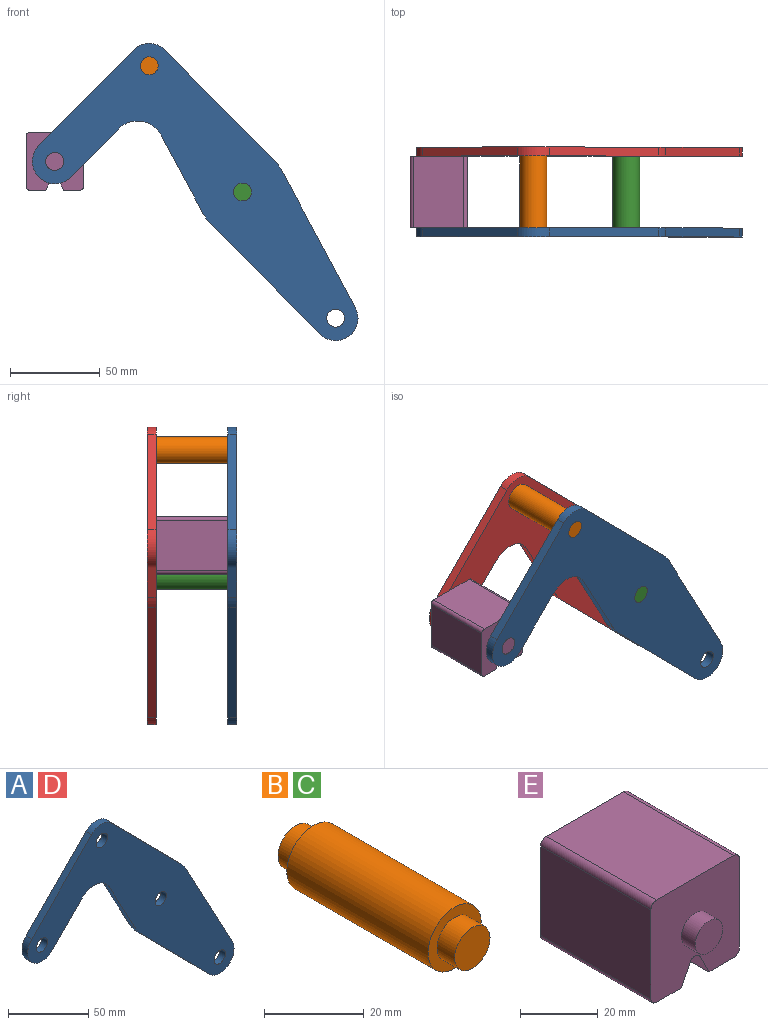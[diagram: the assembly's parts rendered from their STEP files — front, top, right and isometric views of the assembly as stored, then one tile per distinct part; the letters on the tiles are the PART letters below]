
ASSEMBLY  parts=5 mates=3
PART A: 18 faces, bbox 181.7x5x165.8 mm
  f0: plane 43.49x23.35mm, normal (-0.88,0,-0.47), area 246.8mm2, adj f1,f14,f16,f17
  f1: cylinder r=25mm len=5.75mm, axis (0,1,0), area 35.8mm2, adj f0,f2,f16,f17
  f2: plane 61.6x60.87mm, normal (-0.71,0,-0.7), area 433mm2, adj f1,f3,f16,f17
  f3: cylinder r=12.5mm len=21.39mm, axis (0,1,0), area 178.4mm2, adj f2,f4,f16,f17
  f4: plane 76.3x40.96mm, normal (0.88,0,0.47), area 433mm2, adj f3,f5,f16,f17
  f5: cylinder r=25mm len=5.75mm, axis (0,1,0), area 35.8mm2, adj f4,f6,f16,f17
  f6: plane 61.6x60.87mm, normal (0.71,0,0.7), area 433mm2, adj f5,f7,f16,f17
  f7: cylinder r=12.5mm len=17.78mm, axis (0,1,0), area 98.9mm2, adj f6,f8,f16,f17
  f8: plane 53.35x52.71mm, normal (-0.71,0,0.7), area 375mm2, adj f7,f9,f16,f17
  f9: cylinder r=12.5mm len=21.39mm, axis (0,1,0), area 196.3mm2, adj f8,f10,f16,f17
  f10: plane 26.86x26.54mm, normal (0.71,0,-0.7), area 188.8mm2, adj f9,f14,f16,f17
  f11: cylinder r=5mm len=10mm, axis (0,1,0), area 157.1mm2, adj f16,f17
  f12: cylinder r=5mm len=10mm, axis (0,1,0), area 157.1mm2, adj f16,f17
  f13: cylinder r=5mm len=10mm, axis (0,1,0), area 157.1mm2, adj f16,f17
  f14: cylinder r=15mm len=23.89mm, axis (0,1,0), area 140.2mm2, adj f0,f10,f16,f17
  f15: cylinder r=5mm len=10mm, axis (0,1,0), area 157.1mm2, adj f16,f17
  f16: plane 181.66x165.78mm, normal (0,-1,0), area 8710.1mm2, adj f0,f1,f2,f3,f4,f5,f6,f7
  f17: plane 181.66x165.78mm, normal (0,1,0), area 8710.1mm2, adj f0,f1,f2,f3,f4,f5,f6,f7
PART B: 7 faces, bbox 15x50x15 mm
  f0: cylinder r=7.5mm len=40mm, axis (0,-1,0), area 1885mm2, adj f2,f5
  f1: cylinder r=5mm len=10mm, axis (0,1,0), area 157.1mm2, adj f2,f3
  f2: plane 15x15mm, normal (0,-1,0), area 98.2mm2, adj f0,f1
  f3: plane 10x10mm, normal (0,-1,0), area 78.5mm2, adj f1
  f4: cylinder r=5mm len=10mm, axis (0,-1,0), area 157.1mm2, adj f5,f6
  f5: plane 15x15mm, normal (0,1,0), area 98.2mm2, adj f0,f4
  f6: plane 10x10mm, normal (0,1,0), area 78.5mm2, adj f4
PART C: same geometry as B
PART D: same geometry as A
PART E: 18 faces, bbox 32.1x50x32.1 mm
  f0: plane 40x28.08mm, normal (1,0,0), area 1123.1mm2, adj f4,f10,f13,f14
  f1: plane 40x9.04mm, normal (0,0,-1), area 361.6mm2, adj f2,f4,f10,f14
  f2: plane 40x6.42mm, normal (-0.89,0,-0.45), area 287.2mm2, adj f1,f4,f10,f15
  f3: plane 40x6.42mm, normal (0.89,0,-0.45), area 287.2mm2, adj f4,f5,f10,f15
  f4: plane 32.08x32.08mm, normal (0,-1,0), area 900.6mm2, adj f0,f1,f2,f3,f5,f6,f7,f9
  f5: plane 40x9.04mm, normal (0,0,-1), area 361.6mm2, adj f3,f4,f10,f16
  f6: plane 40x28.08mm, normal (0,0,1), area 1123.1mm2, adj f4,f10,f13,f17
  f7: plane 40x28.08mm, normal (-1,0,0), area 1123.1mm2, adj f4,f10,f16,f17
  f8: plane 10x10mm, normal (0,-1,0), area 78.5mm2, adj f9
  f9: cylinder r=5mm len=10mm, axis (0,1,0), area 157.1mm2, adj f4,f8
  f10: plane 32.08x32.08mm, normal (0,1,0), area 900.6mm2, adj f0,f1,f2,f3,f5,f6,f7,f12
  f11: plane 10x10mm, normal (0,1,0), area 78.5mm2, adj f12
  f12: cylinder r=5mm len=10mm, axis (0,-1,0), area 157.1mm2, adj f10,f11
  f13: cylinder r=2mm len=40mm, axis (0,1,0), area 125.7mm2, adj f0,f4,f6,f10
  f14: cylinder r=2mm len=40mm, axis (0,-1,0), area 125.7mm2, adj f0,f1,f4,f10
  f15: cylinder r=2mm len=40mm, axis (0,1,0), area 177.1mm2, adj f2,f3,f4,f10
  f16: cylinder r=2mm len=40mm, axis (0,1,0), area 125.7mm2, adj f4,f5,f7,f10
  f17: cylinder r=2mm len=40mm, axis (0,-1,0), area 125.7mm2, adj f4,f6,f7,f10
PLACE A t=(14.21,3.43,20.66)mm fixed
PLACE B t=(14.21,3.43,20.66)mm
PLACE C t=(66.18,3.43,-49.73)mm
PLACE D t=(14.21,48.43,20.66)mm
PLACE E t=(14.21,3.43,20.66)mm
MATE revolute E.f9 <-> A.f9  axis (0,-1,0) through (-90.48,3.43,37.7)mm
MATE fastened A.f1 <-> C.f0  axis (0,1,0) through (14.21,3.43,20.66)mm
MATE fastened D.f7 <-> B.f0  axis (0,1,0) through (-37.77,43.43,91.05)mm
